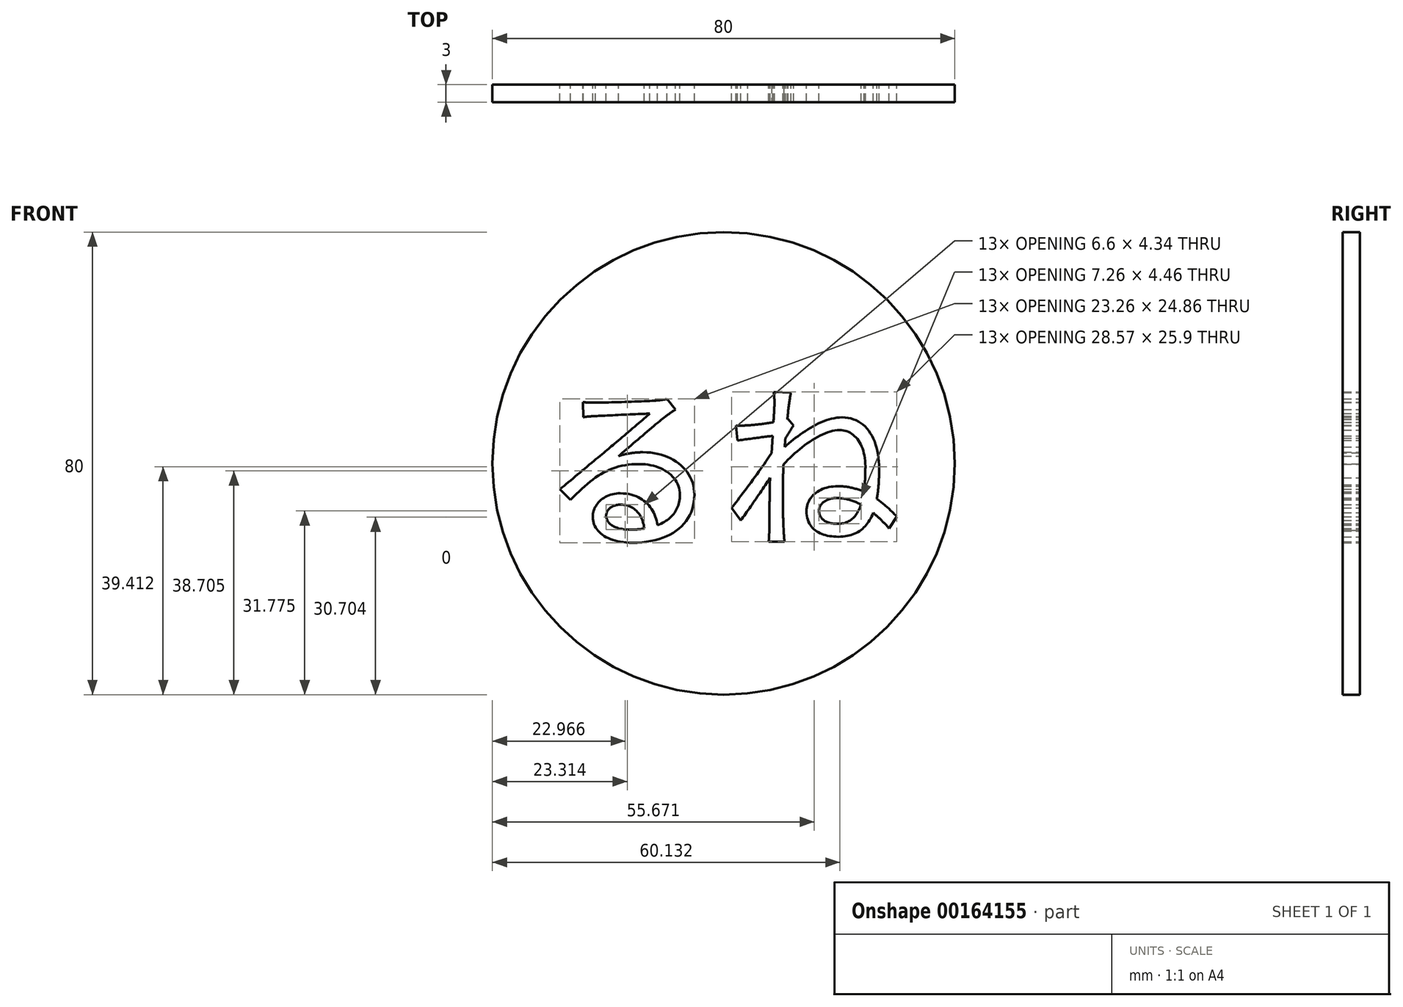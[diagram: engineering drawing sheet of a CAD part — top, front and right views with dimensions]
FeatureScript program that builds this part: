
annotation { "Feature Type Name" : "Feature", "Feature Type Description" : "" }
export const myFeature = defineFeature(function(context is Context, id is Id, definition is map)
    precondition{}
    {
        {
            var Q0;
            Q0=qCreatedBy(makeId("Front.planeOp"),FACE);
            var sketch = newSketch(context, id + "F0", { "sketchPlane" : qUnion([Q0])});
            skCircle(sketch, "E0", {"center": v(0, 0) * mm, "radius": 40 * mm});
            skText(sketch, "E1", { "text": "るね", "fontName": "NotoSansCJKjp-Regular.otf"});
            const initialGuessF0  = {"E1": [-0.0319, -0.0125, 1, 0, 0.02263]};
            skSetInitialGuess(sketch, initialGuessF0);
            skSolve(sketch);
        }
        {
            var Q0;
            Q0=makeQuery(id+"F0.imprint","IMPRINT",FACE,{"disambiguationData":[TD([[makeQuery(id+"F0.imprint","IMPRINT",EDGE,{"derivedFrom":sQuery(id+"F0.wireOp",EDGE,"E0")}),1.0]])]});
            var Q1;
            Q1=makeQuery(id+"F0.imprint","IMPRINT",FACE,{"disambiguationData":[TD([[makeQuery(id+"F0.imprint","IMPRINT",EDGE,{"derivedFrom":sQuery(id+"F0.wireOp",EDGE,"E1.sketch_text.stroke-25")}),-1.0]])]});
            var Q2;
            Q2=makeQuery(id+"F0.imprint","IMPRINT",FACE,{"disambiguationData":[TD([[makeQuery(id+"F0.imprint","IMPRINT",EDGE,{"derivedFrom":sQuery(id+"F0.wireOp",EDGE,"E1.sketch_text.stroke-0")}),-1.0]])]});
            extrude(context, id + "F1", {"entities" : qUnion([Q0, Q1, Q2]), "depth" : 3 * mm});
        }
        {
            var Q0;
            Q0=makeQuery(id+"F0.imprint","IMPRINT",FACE,{"disambiguationData":[TD([[makeQuery(id+"F0.imprint","IMPRINT",EDGE,{"derivedFrom":sQuery(id+"F0.wireOp",EDGE,"E1.sketch_text.stroke-0")}),1.0]])]});
            var Q1;
            Q1=makeQuery(id+"F0.imprint","IMPRINT",FACE,{"disambiguationData":[TD([[makeQuery(id+"F0.imprint","IMPRINT",EDGE,{"derivedFrom":sQuery(id+"F0.wireOp",EDGE,"E1.sketch_text.stroke-25")}),1.0]])]});
            extrude(context, id + "F2", {"entities" : qUnion([Q0, Q1]), "depth" : 3 * mm});
        }
    });
